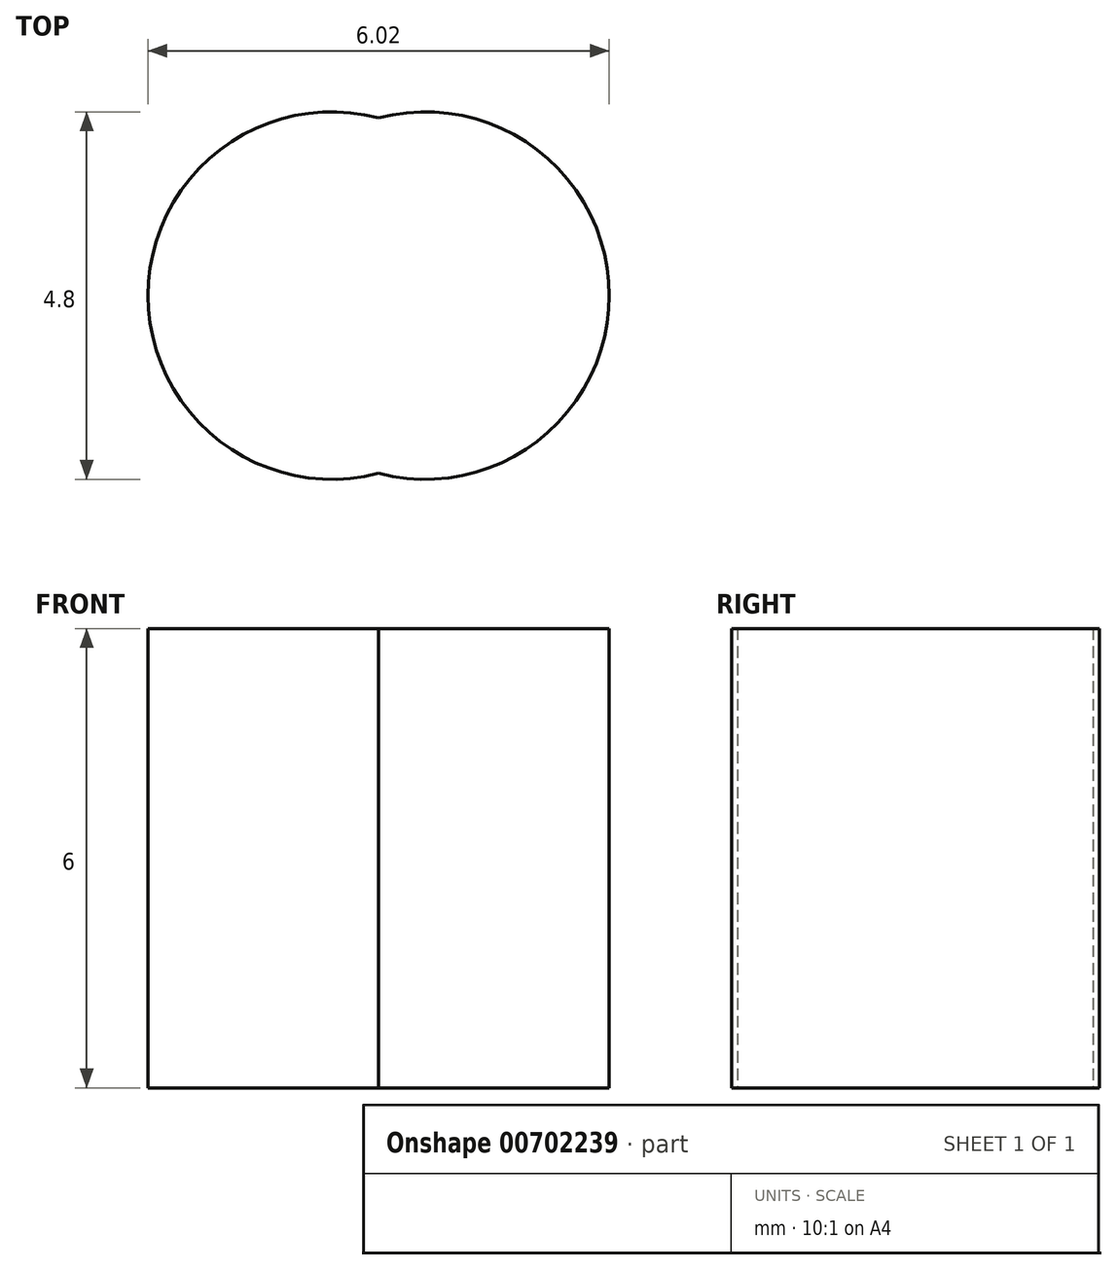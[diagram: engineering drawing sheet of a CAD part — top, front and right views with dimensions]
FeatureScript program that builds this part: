
annotation { "Feature Type Name" : "Feature", "Feature Type Description" : "" }
export const myFeature = defineFeature(function(context is Context, id is Id, definition is map)
    precondition{}
    {
        {
            var Q0;
            Q0=qCreatedBy(makeId("Top.planeOp"),FACE);
            var sketch = newSketch(context, id + "F0", { "sketchPlane" : qUnion([Q0])});
            skCircle(sketch, "E0", {"center": v(2.41, 0) * mm, "radius": 2.4 * mm});
            skCircle(sketch, "E1", {"center": v(1.2, 0) * mm, "radius": 2.4 * mm});
            skSolve(sketch);
        }
        {
            var Q0;
            {var subQ0=sQuery(id+"F0.wireOp",EDGE,"E1");var subQ1=sQuery(id+"F0.wireOp",EDGE,"E0");var subQ2=makeQuery(id+"F0.imprint","INTERSECT",VERTEX,{"disambiguationData":[OD(0.0)],"derivedFrom":[subQ1,subQ0]});Q0=makeQuery(id+"F0.imprint","IMPRINT",FACE,{"disambiguationData":[TD([[makeQuery(id+"F0.imprint","IMPRINT",EDGE,{"disambiguationData":[TD([[subQ2,1.0]])],"derivedFrom":subQ1}),-1.0]])]});}
            var Q1;
            {var subQ0=sQuery(id+"F0.wireOp",EDGE,"E1");var subQ1=sQuery(id+"F0.wireOp",EDGE,"E0");var subQ2=makeQuery(id+"F0.imprint","INTERSECT",VERTEX,{"disambiguationData":[OD(0.0)],"derivedFrom":[subQ1,subQ0]});Q1=makeQuery(id+"F0.imprint","IMPRINT",FACE,{"disambiguationData":[TD([[makeQuery(id+"F0.imprint","IMPRINT",EDGE,{"disambiguationData":[TD([[subQ2,-1.0]])],"derivedFrom":subQ1}),1.0]])]});}
            var Q2;
            {var subQ0=sQuery(id+"F0.wireOp",EDGE,"E1");var subQ1=sQuery(id+"F0.wireOp",EDGE,"E0");var subQ2=makeQuery(id+"F0.imprint","INTERSECT",VERTEX,{"disambiguationData":[OD(0.0)],"derivedFrom":[subQ1,subQ0]});Q2=makeQuery(id+"F0.imprint","IMPRINT",FACE,{"disambiguationData":[TD([[makeQuery(id+"F0.imprint","IMPRINT",EDGE,{"disambiguationData":[TD([[subQ2,1.0]])],"derivedFrom":subQ1}),1.0]])]});}
            extrude(context, id + "F1", {"entities" : qUnion([Q0, Q1, Q2]), "depth" : 6 * mm, "offsetDistance" : 25 * mm});
        }
    });
